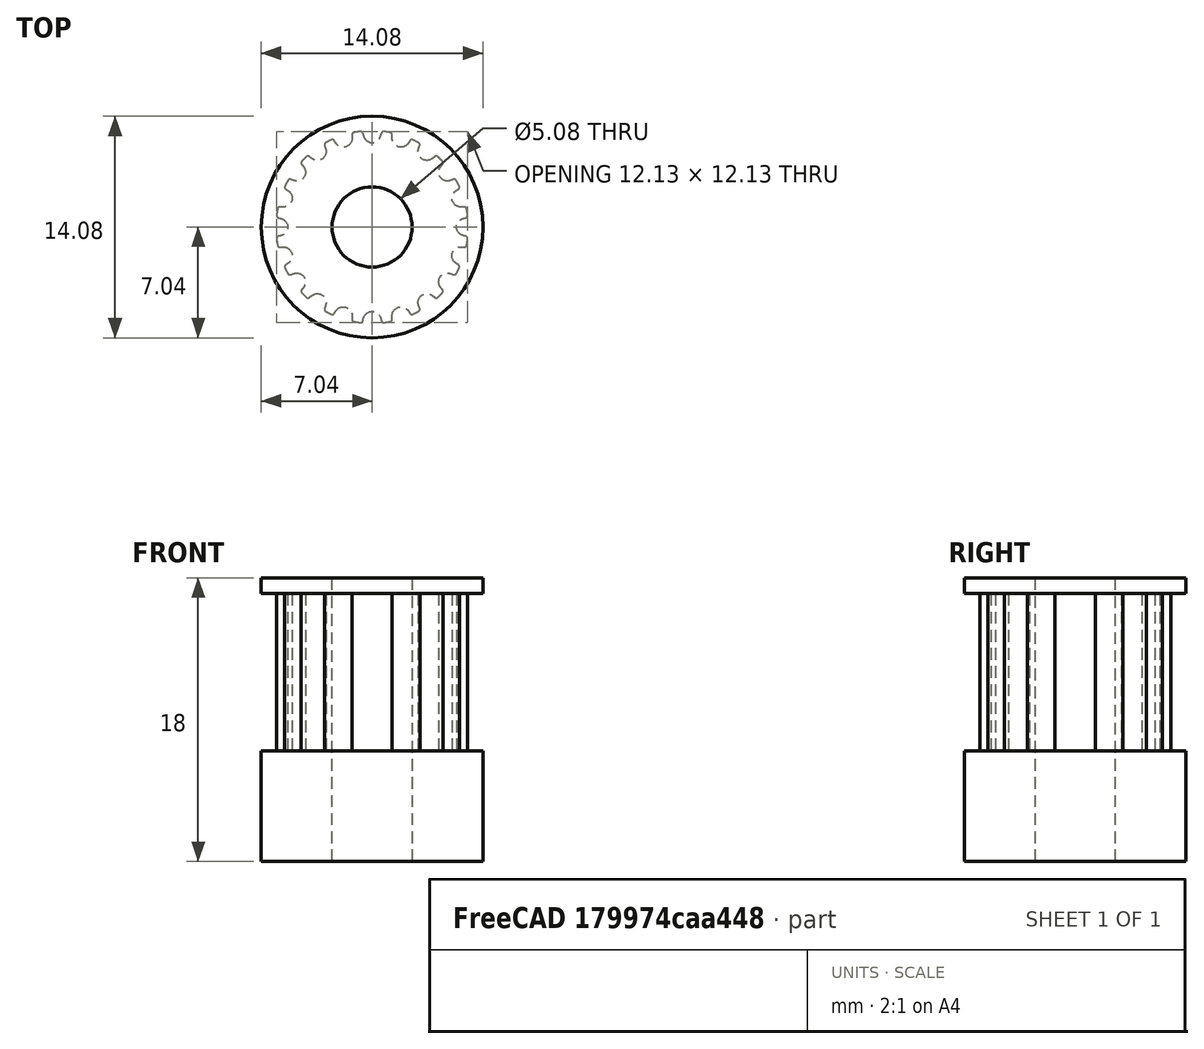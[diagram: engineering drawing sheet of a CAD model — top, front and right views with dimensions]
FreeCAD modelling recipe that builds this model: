
FCSTD DOCUMENT  (FreeCAD 0.20R29177 (Git))
Label: GT2_20_L10
License: All rights reserved
LicenseURL: http://en.wikipedia.org/wiki/All_rights_reserved
objects: Sketcher::SketchObject×3, PartDesign::Pad×2, Part::FeaturePython×1, PartDesign::FeatureBase×1, PartDesign::Pocket×1, PartDesign::Body×1
note: 12 computed .brp shape members not serialized (recipe doc carries the construction recipe); baked Part::Feature solids carry a one-line shape summary decoded from their .brp

FEATURE [Part::FeaturePython] timinggear  # WARN: FeaturePython — macro-defined, semantics opaque (R4)
  AttacherType = Attacher::AttachEngine3D
  h = 0.75
  height = 10
  offset = 0.4
  pitch = 2
  r0 = 0.555
  r1 = 1
  rs = 0.15
  teeth = 20
  type = 0
  u = 0.254
  version = 0.0.3
FEATURE [PartDesign::FeatureBase] BaseFeature
  BaseFeature = -> timinggear
FEATURE [Sketcher::SketchObject] Sketch
  FullyConstrained = false
  MapMode = 5
  Placement = pos=(0,0,0) rot=(1,0,0;3.14159rad)
  Support = -> [BaseFeature]
  sketch-geometry (1):
    g0: Circle CenterX=0 CenterY=0 CenterZ=0 NormalX=0 NormalY=0 NormalZ=1 AngleXU=0 Radius=7.03764
  constraints (1):
    c: Coincident(g0,g-1)
FEATURE [PartDesign::Pad] Pad
  BaseFeature = -> BaseFeature
  Direction = (0,0,-1)
  Length = 7
  Length2 = 10
  Profile = -> Sketch
  ReferenceAxis = -> Sketch [N_Axis]
  Type = 0
FEATURE [Sketcher::SketchObject] Sketch001
  FullyConstrained = false
  MapMode = 5
  Placement = pos=(0,0,10) rot=(0,0,1;0rad)
  Support = -> [Pad]
  sketch-geometry (1):
    g0: Circle CenterX=0 CenterY=0 CenterZ=0 NormalX=0 NormalY=0 NormalZ=1 AngleXU=0 Radius=7.03729
  constraints (1):
    c: Coincident(g0,g-1)
FEATURE [PartDesign::Pad] Pad001
  BaseFeature = -> Pad
  Direction = (0,0,1)
  Length = 1
  Length2 = 10
  Profile = -> Sketch001
  ReferenceAxis = -> Sketch001 [N_Axis]
  Type = 0
FEATURE [Sketcher::SketchObject] Sketch002
  FullyConstrained = false
  MapMode = 5
  Placement = pos=(0,0,11) rot=(0,0,1;0rad)
  Support = -> [Pad001]
  sketch-geometry (1):
    g0: Circle CenterX=0 CenterY=0 CenterZ=0 NormalX=0 NormalY=0 NormalZ=1 AngleXU=0 Radius=2.54179
  constraints (1):
    c: Coincident(g0,g-1)
FEATURE [PartDesign::Pocket] Pocket
  BaseFeature = -> Pad001
  Direction = (0,0,-1)
  Length = 18
  Length2 = 5
  Profile = -> Sketch002
  ReferenceAxis = -> Sketch002 [N_Axis]
  Type = 0
FEATURE [PartDesign::Body] Body
  BaseFeature = -> timinggear
  Group = -> [BaseFeature,Sketch,Pad,Sketch001,Pad001,Sketch002,Pocket]
  Origin = -> Origin
  Tip = -> Pocket
